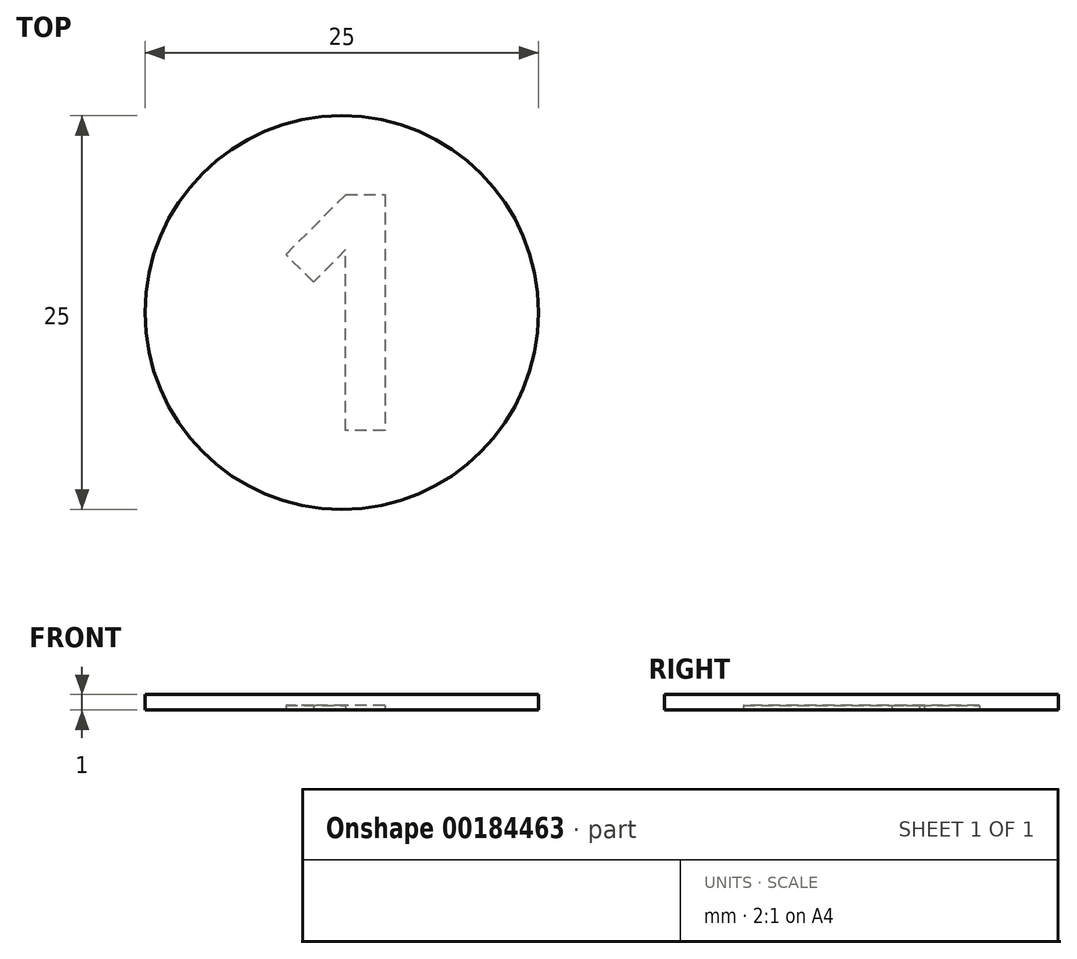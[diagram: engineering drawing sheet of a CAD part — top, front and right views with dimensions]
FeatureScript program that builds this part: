
annotation { "Feature Type Name" : "Feature", "Feature Type Description" : "" }
export const myFeature = defineFeature(function(context is Context, id is Id, definition is map)
    precondition{}
    {
        {
            var Q0;
            Q0=qCreatedBy(makeId("Front.planeOp"),FACE);
            var sketch = newSketch(context, id + "F3", { "sketchPlane" : qUnion([Q0])});
            skLineSegment(sketch, "E0.bottom", {"start": v(0, 0) * mm, "end": v(-12.5, 0) * mm});
            skLineSegment(sketch, "E0.top", {"start": v(0, 1) * mm, "end": v(-12.5, 1) * mm});
            skLineSegment(sketch, "E0.left", {"start": v(0, 0) * mm, "end": v(0, 1) * mm});
            skLineSegment(sketch, "E0.right", {"start": v(-12.5, 0) * mm, "end": v(-12.5, 1) * mm});
            skSolve(sketch);
        }
        {
            var Q0;
            Q0=makeQuery(id+"F3.imprint","IMPRINT",FACE,{"disambiguationData":[TD([[makeQuery(id+"F3.imprint","IMPRINT",EDGE,{"derivedFrom":sQuery(id+"F3.wireOp",EDGE,"E0.bottom")}),-1.0]])]});
            var Q1;
            Q1=sQuery(id+"F3.wireOp",EDGE,"E0.left");
            revolve(context, id + "F4", {"entities" : qUnion([Q0]), "axis" : qUnion([Q1]), "revolveType" : RevolveType.FULL});
        }
        {
            var Q0;
            Q0=qCreatedBy(makeId("Top.planeOp"),FACE);
            var sketch = newSketch(context, id + "F0", { "sketchPlane" : qUnion([Q0])});
            skText(sketch, "E1", { "text": "1", "fontName": "AllertaStencil-Regular.ttf"});
            const initialGuessF0  = {"E1": [-0.00414, -0.0075, 1, 0, 0.015]};
            skSetInitialGuess(sketch, initialGuessF0);
            skSolve(sketch);
        }
        {
            var Q0;
            Q0 = qSketchRegion(id + "F0", true);
            extrude(context, id + "F1", {"entities" : qUnion([Q0]), "depth" : 0.3 * mm});
        }
        {
            var Q0;
            Q0=makeQuery(id+"F1.opExtrude","SWEPT_BODY",BODY,{"disambiguationData":[OSD([sQuery(id+"F0.wireOp",EDGE,"E1.sketch_text.stroke-0"),sQuery(id+"F0.wireOp",EDGE,"E1.sketch_text.stroke-1"),sQuery(id+"F0.wireOp",EDGE,"E1.sketch_text.stroke-2"),sQuery(id+"F0.wireOp",EDGE,"E1.sketch_text.stroke-3"),sQuery(id+"F0.wireOp",EDGE,"E1.sketch_text.stroke-4"),sQuery(id+"F0.wireOp",EDGE,"E1.sketch_text.stroke-5"),sQuery(id+"F0.wireOp",EDGE,"E1.sketch_text.stroke-6")])]});
            var Q1;
            Q1=makeQuery(id+"F4.opRevolve","SWEPT_BODY",BODY,{"disambiguationData":[OSD([sQuery(id+"F3.wireOp",EDGE,"E0.bottom"),sQuery(id+"F3.wireOp",EDGE,"E0.top"),sQuery(id+"F3.wireOp",EDGE,"E0.left"),sQuery(id+"F3.wireOp",EDGE,"E0.right")])]});
            booleanBodies(context, id + "F2", {"operationType" : BooleanOperationType.SUBTRACTION, "tools" : qUnion([Q0]), "targets" : qUnion([Q1])});
        }
    });
